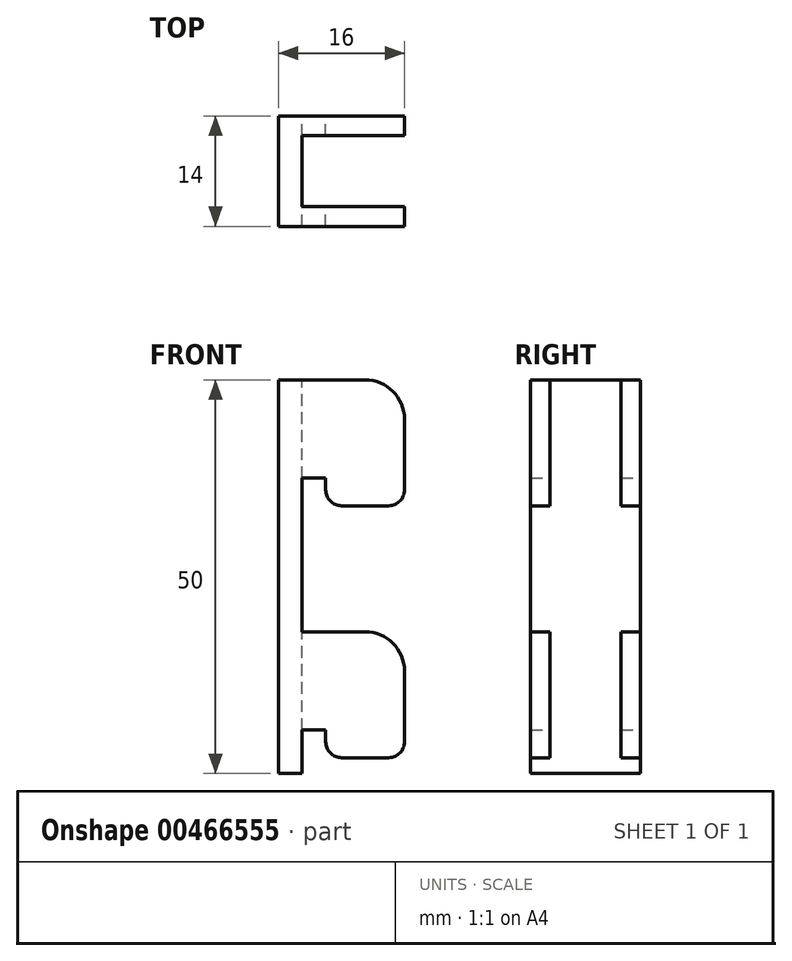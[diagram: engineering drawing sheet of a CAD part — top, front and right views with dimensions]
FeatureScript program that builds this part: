
annotation { "Feature Type Name" : "Feature", "Feature Type Description" : "" }
export const myFeature = defineFeature(function(context is Context, id is Id, definition is map)
    precondition{}
    {
        {
            assignVariable(context, id + "F0", {"name" : "Width", "anyValue" : 14});
        }
        {
            var Q0;
            Q0=qCreatedBy(makeId("Front.planeOp"),FACE);
            var sketch = newSketch(context, id + "F1", { "sketchPlane" : qUnion([Q0])});
            skLineSegment(sketch, "E0.bottom", {"start": v(0, 50) * mm, "end": v(3, 50) * mm});
            skLineSegment(sketch, "E0.top", {"start": v(0, 0) * mm, "end": v(3, 0) * mm});
            skLineSegment(sketch, "E0.left", {"start": v(0, 50) * mm, "end": v(0, 0) * mm});
            skLineSegment(sketch, "E0.right", {"start": v(3, 50) * mm, "end": v(3, 0) * mm});
            skLineSegment(sketch, "E1.bottom", {"start": v(3, 50) * mm, "end": v(6, 50) * mm});
            skLineSegment(sketch, "E1.top", {"start": v(3, 37.5) * mm, "end": v(6, 37.5) * mm});
            skLineSegment(sketch, "E1.left", {"start": v(3, 50) * mm, "end": v(3, 37.5) * mm});
            skLineSegment(sketch, "E1.right", {"start": v(6, 50) * mm, "end": v(6, 37.5) * mm});
            skLineSegment(sketch, "E2.bottom", {"start": v(3, 5.5) * mm, "end": v(6, 5.5) * mm});
            skLineSegment(sketch, "E2.top", {"start": v(3, 18) * mm, "end": v(6, 18) * mm});
            skLineSegment(sketch, "E2.left", {"start": v(3, 18) * mm, "end": v(3, 5.5) * mm});
            skLineSegment(sketch, "E2.right", {"start": v(6, 18) * mm, "end": v(6, 5.5) * mm});
            skLineSegment(sketch, "E3.bottom", {"start": v(6, 50) * mm, "end": v(11, 50) * mm});
            skLineSegment(sketch, "E3.top", {"start": v(8, 34) * mm, "end": v(14, 34) * mm});
            skLineSegment(sketch, "E3.left", {"start": v(6, 50) * mm, "end": v(6, 36) * mm});
            skLineSegment(sketch, "E3.right", {"start": v(16, 45) * mm, "end": v(16, 36) * mm});
            skLineSegment(sketch, "E4.bottom", {"start": v(6, 18) * mm, "end": v(11, 18) * mm});
            skLineSegment(sketch, "E4.top", {"start": v(8, 2) * mm, "end": v(14, 2) * mm});
            skLineSegment(sketch, "E4.left", {"start": v(6, 18) * mm, "end": v(6, 4) * mm});
            skLineSegment(sketch, "E4.right", {"start": v(16, 13) * mm, "end": v(16, 4) * mm});
            skPoint(sketch, "E5.visualSharp", {"position": v(16, 50) * mm});
            skArc(sketch, "E5.filletArc", {"start": v(16, 45) * mm, "mid": v(14.54, 48.54) * mm, "end": v(11, 50) * mm});
            skPoint(sketch, "E6.visualSharp", {"position": v(16, 18) * mm});
            skArc(sketch, "E6.filletArc", {"start": v(16, 13) * mm, "mid": v(14.54, 16.54) * mm, "end": v(11, 18) * mm});
            skPoint(sketch, "E7.visualSharp", {"position": v(16, 2) * mm});
            skArc(sketch, "E7.filletArc", {"start": v(14, 2) * mm, "mid": v(15.41, 2.59) * mm, "end": v(16, 4) * mm});
            skPoint(sketch, "E8.visualSharp", {"position": v(6, 2) * mm});
            skArc(sketch, "E8.filletArc", {"start": v(6, 4) * mm, "mid": v(6.59, 2.59) * mm, "end": v(8, 2) * mm});
            skPoint(sketch, "E9.visualSharp", {"position": v(16, 34) * mm});
            skArc(sketch, "E9.filletArc", {"start": v(14, 34) * mm, "mid": v(15.41, 34.59) * mm, "end": v(16, 36) * mm});
            skPoint(sketch, "E10.visualSharp", {"position": v(6, 34) * mm});
            skArc(sketch, "E10.filletArc", {"start": v(6, 36) * mm, "mid": v(6.59, 34.59) * mm, "end": v(8, 34) * mm});
            skSolve(sketch);
        }
        {
            var Q0;
            Q0=qSketchRegion(id+"F1",true);
            extrude(context, id + "F2", {"entities" : qUnion([Q0]), "endBound" : BoundingType.SYMMETRIC, "depth" : (getVariable(context, 'Width')) * mm});
        }
        {
            var Q0;
            {var subQ0=sQuery(id+"F1.wireOp",EDGE,"E0.right");Q0=makeQuery(id+"F2.opExtrude","SWEPT_FACE",FACE,{"disambiguationData":[OSD([subQ0]),TDD([makeQuery(id+"F1.imprint","IMPRINT",EDGE,{"disambiguationData":[TD([[makeQuery(id+"F1.imprint","INTERSECT",VERTEX,{"derivedFrom":[subQ0,sQuery(id+"F1.wireOp",EDGE,"E1.top"),sQuery(id+"F1.wireOp",EDGE,"E1.left")]}),-1.0]])],"derivedFrom":subQ0})])]});}
            var sketch = newSketch(context, id + "F3", { "sketchPlane" : qUnion([Q0])});
            skLineSegment(sketch, "E11.bottom", {"start": v(-4.5, 0) * mm, "end": v(4.5, 0) * mm});
            skLineSegment(sketch, "E11.top", {"start": v(-4.5, 50) * mm, "end": v(4.5, 50) * mm});
            skLineSegment(sketch, "E11.left", {"start": v(-4.5, 0) * mm, "end": v(-4.5, 50) * mm});
            skLineSegment(sketch, "E11.right", {"start": v(4.5, 0) * mm, "end": v(4.5, 50) * mm});
            skSolve(sketch);
        }
        {
            var Q0;
            Q0=qSketchRegion(id+"F3",true);
            extrude(context, id + "F4", {"entities" : qUnion([Q0]), "operationType" : NewBodyOperationType.REMOVE, "endBound" : BoundingType.THROUGH_ALL, "depth" : 25 * mm});
        }
    });
